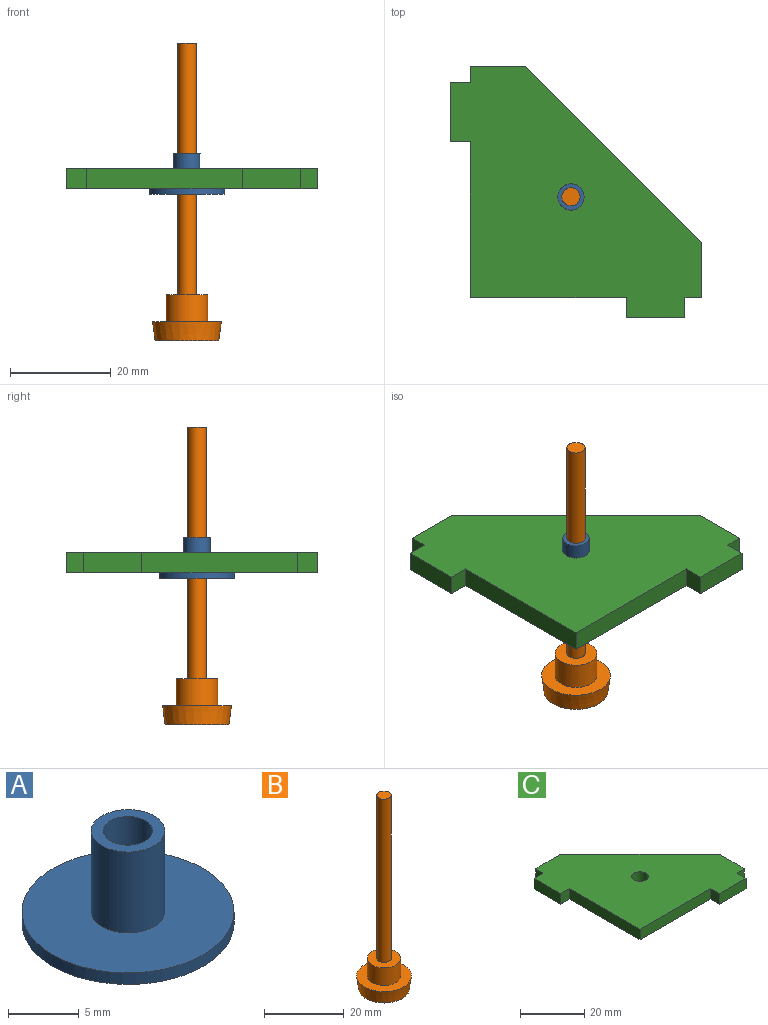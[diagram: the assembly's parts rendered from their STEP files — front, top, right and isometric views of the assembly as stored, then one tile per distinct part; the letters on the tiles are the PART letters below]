
ASSEMBLY  parts=3 mates=2
PART A: 6 faces, bbox 15x15x8 mm
  f0: plane 5.2x5.2mm, normal (0,0,1), area 11.6mm2, adj f1,f5
  f1: cylinder r=1.75mm len=8mm, axis (0,0,-1), area 88mm2, adj f0,f2
  f2: plane 15x15mm, normal (0,0,-1), area 167.1mm2, adj f1,f3
  f3: cylinder r=7.5mm len=15mm, axis (0,0,-1), area 47.1mm2, adj f2,f4
  f4: plane 15x15mm, normal (0,0,1), area 155.5mm2, adj f3,f5
  f5: cylinder r=2.6mm len=7mm, axis (0,0,-1), area 114.4mm2, adj f0,f4
PART B: 7 faces, bbox 13.7x13.7x59.2 mm
  f0: plane 3.6x3.6mm, normal (0,0,1), area 10.2mm2, adj f6
  f1: plane 12.7x12.7mm, normal (0,0,-1), area 126.7mm2, adj f2
  f2: cone r=6.85mm half-angle=7.5deg, axis (0,0,1), area 158.9mm2, adj f1,f3
  f3: plane 13.7x13.7mm, normal (0,0,1), area 93.3mm2, adj f2,f4
  f4: cylinder r=4.15mm len=8.3mm, axis (0,0,1), area 140.8mm2, adj f3,f5
  f5: plane 8.3x8.3mm, normal (0,0,1), area 43.9mm2, adj f4,f6
  f6: cylinder r=1.8mm len=50mm, axis (0,0,1), area 565.5mm2, adj f0,f5
PART C: 16 faces, bbox 50x50x4 mm
  f0: plane 50x50mm, normal (0,0,-1), area 1575.6mm2, adj f1,f2,f3,f4,f5,f6,f7,f8
  f1: plane 4x4mm, normal (-1,0,0), area 16mm2, adj f0,f2,f13,f15
  f2: plane 11.67x4mm, normal (0,-1,0), area 46.7mm2, adj f0,f1,f3,f15
  f3: plane 4x4mm, normal (1,0,0), area 16mm2, adj f0,f2,f4,f15
  f4: plane 4x3.33mm, normal (0,-1,0), area 13.3mm2, adj f0,f3,f5,f15
  f5: plane 11x4mm, normal (1,0,0), area 44mm2, adj f0,f4,f6,f15
  f6: plane 35x35mm, normal (0.71,0.71,0), area 198mm2, adj f0,f5,f7,f15
  f7: plane 11x4mm, normal (0,1,0), area 44mm2, adj f0,f6,f8,f15
  f8: plane 4x3.33mm, normal (-1,0,0), area 13.3mm2, adj f0,f7,f9,f15
  f9: plane 4x4mm, normal (0,1,0), area 16mm2, adj f0,f8,f10,f15
  f10: plane 11.67x4mm, normal (-1,0,0), area 46.7mm2, adj f0,f9,f11,f15
  f11: plane 4x4mm, normal (0,-1,0), area 16mm2, adj f0,f10,f12,f15
  f12: plane 31x4mm, normal (-1,0,0), area 124mm2, adj f0,f11,f13,f15
  f13: plane 31x4mm, normal (0,-1,0), area 124mm2, adj f0,f1,f12,f15
  f14: cylinder r=2.6mm len=5.2mm, axis (0,0,1), area 65.3mm2, adj f0,f15
  f15: plane 50x50mm, normal (0,0,1), area 1575.6mm2, adj f1,f2,f3,f4,f5,f6,f7,f8
PLACE A t=(-161,-161,-64)mm
PLACE B rot(axis=(0,0,-1),74.4deg) t=(-161,-161,-69.2)mm
PLACE C at identity fixed
MATE revolute A.f1 <-> C.f14  axis (0,0,1) through (-161,-161,-64)mm
MATE revolute B.f2 <-> A.f1  axis (0,0,1) through (-161,-161,-85)mm
